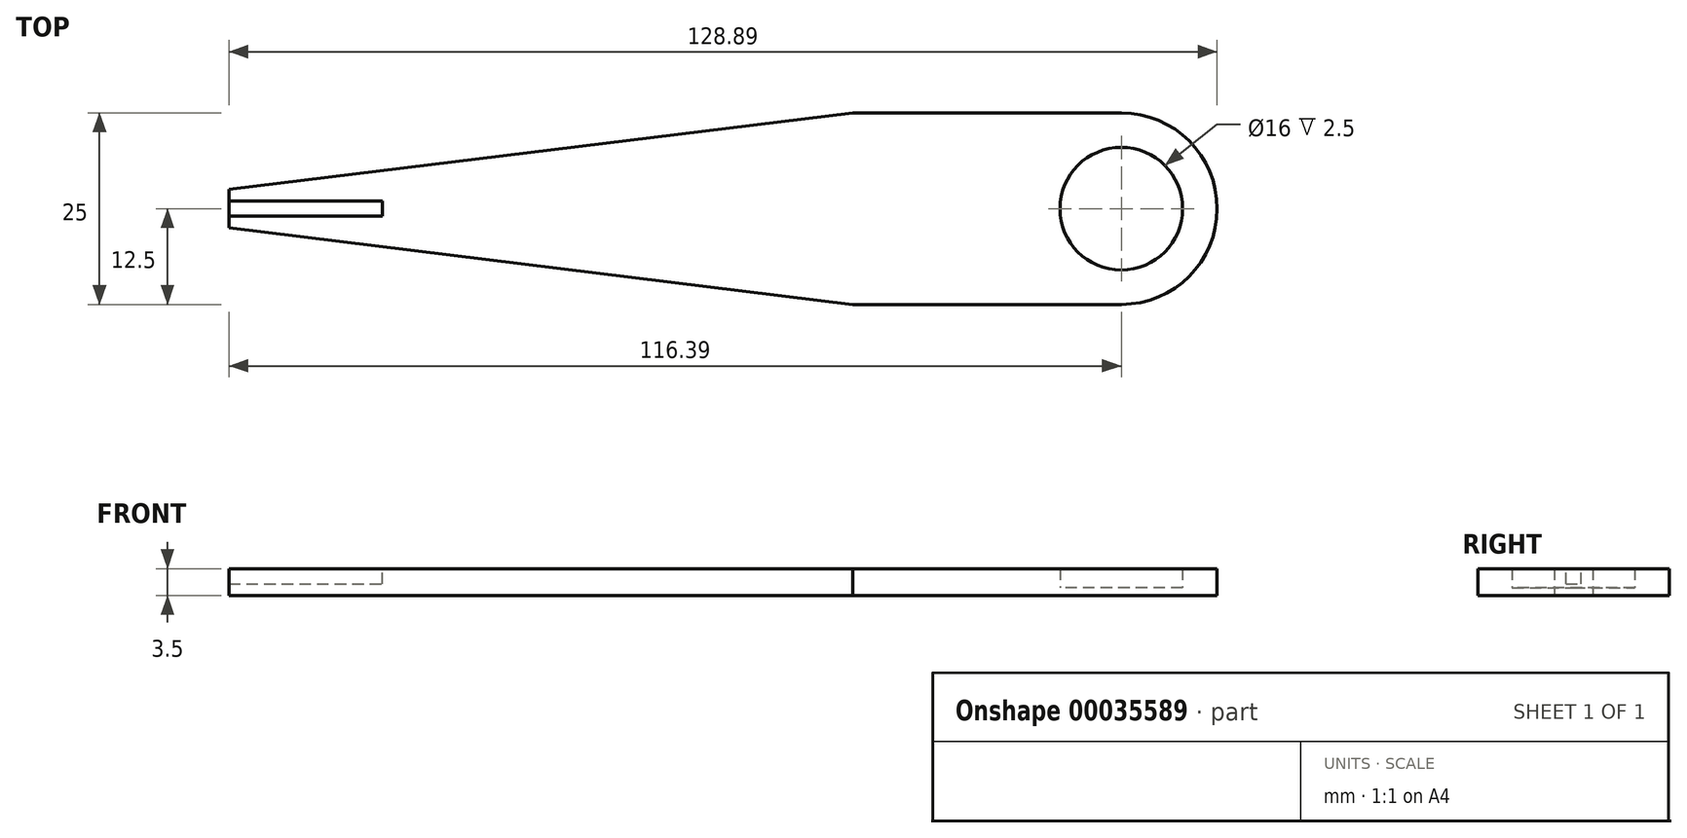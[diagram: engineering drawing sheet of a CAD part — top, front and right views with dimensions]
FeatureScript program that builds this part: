
annotation { "Feature Type Name" : "Feature", "Feature Type Description" : "" }
export const myFeature = defineFeature(function(context is Context, id is Id, definition is map)
    precondition{}
    {
        {
            var Q0;
            Q0=qCreatedBy(makeId("Top.planeOp"),FACE);
            var sketch = newSketch(context, id + "F0", { "sketchPlane" : qUnion([Q0])});
            skCircle(sketch, "E0", {"center": v(0, 0) * mm, "radius": 8 * mm});
            skCircle(sketch, "E1", {"center": v(0, 0) * mm, "radius": 12.5 * mm});
            skLineSegment(sketch, "E2", {"start": v(-35, 12.5) * mm, "end": v(0, 12.5) * mm});
            skLineSegment(sketch, "E3", {"start": v(-35, -12.5) * mm, "end": v(0, -12.5) * mm});
            skLineSegment(sketch, "E4", {"start": v(-35, 12.5) * mm, "end": v(-80.23, 12.5) * mm, "construction": true});
            skLineSegment(sketch, "E5", {"start": v(-35, 12.5) * mm, "end": v(-116.39, 2.5) * mm});
            skLineSegment(sketch, "E6", {"start": v(-35, -12.5) * mm, "end": v(-78.86, -12.5) * mm, "construction": true});
            skLineSegment(sketch, "E7", {"start": v(-35, -12.5) * mm, "end": v(-116.39, -2.5) * mm});
            skLineSegment(sketch, "E8", {"start": v(-116.39, -2.5) * mm, "end": v(-116.39, 2.5) * mm});
            skSolve(sketch);
        }
        {
            var Q0;
            Q0=qSketchRegion(id+"F0",true);
            extrude(context, id + "F1", {"entities" : qUnion([Q0]), "depth" : 3.5 * mm});
        }
        {
            var Q0;
            Q0=makeQuery(id+"F0.imprint","IMPRINT",FACE,{"disambiguationData":[TD([[makeQuery(id+"F0.imprint","IMPRINT",EDGE,{"derivedFrom":sQuery(id+"F0.wireOp",EDGE,"E0")}),1.0]])]});
            extrude(context, id + "F2", {"entities" : qUnion([Q0]), "operationType" : NewBodyOperationType.ADD, "depth" : 1 * mm});
        }
        {
            var Q0;
            Q0=makeQuery(id+"F1.opExtrude","CAP_FACE",FACE,{"disambiguationData":[OSD([sQuery(id+"F0.wireOp",EDGE,"E0"),sQuery(id+"F0.wireOp",EDGE,"E1"),sQuery(id+"F0.wireOp",EDGE,"E2"),sQuery(id+"F0.wireOp",EDGE,"E3"),sQuery(id+"F0.wireOp",EDGE,"E5"),sQuery(id+"F0.wireOp",EDGE,"E7"),sQuery(id+"F0.wireOp",EDGE,"E8")])],"isStart":false});
            var sketch = newSketch(context, id + "F3", { "sketchPlane" : qUnion([Q0])});
            skLineSegment(sketch, "E9.bottom", {"start": v(-116.39, 1) * mm, "end": v(-96.39, 1) * mm});
            skLineSegment(sketch, "E9.top", {"start": v(-116.39, -1) * mm, "end": v(-96.39, -1) * mm});
            skLineSegment(sketch, "E9.left", {"start": v(-116.39, 1) * mm, "end": v(-116.39, -1) * mm});
            skLineSegment(sketch, "E9.right", {"start": v(-96.39, 1) * mm, "end": v(-96.39, -1) * mm});
            skSolve(sketch);
        }
        {
            var Q0;
            Q0=qSketchRegion(id+"F3",true);
            extrude(context, id + "F4", {"entities" : qUnion([Q0]), "operationType" : NewBodyOperationType.REMOVE, "oppositeDirection" : true, "depth" : 2 * mm});
        }
    });
